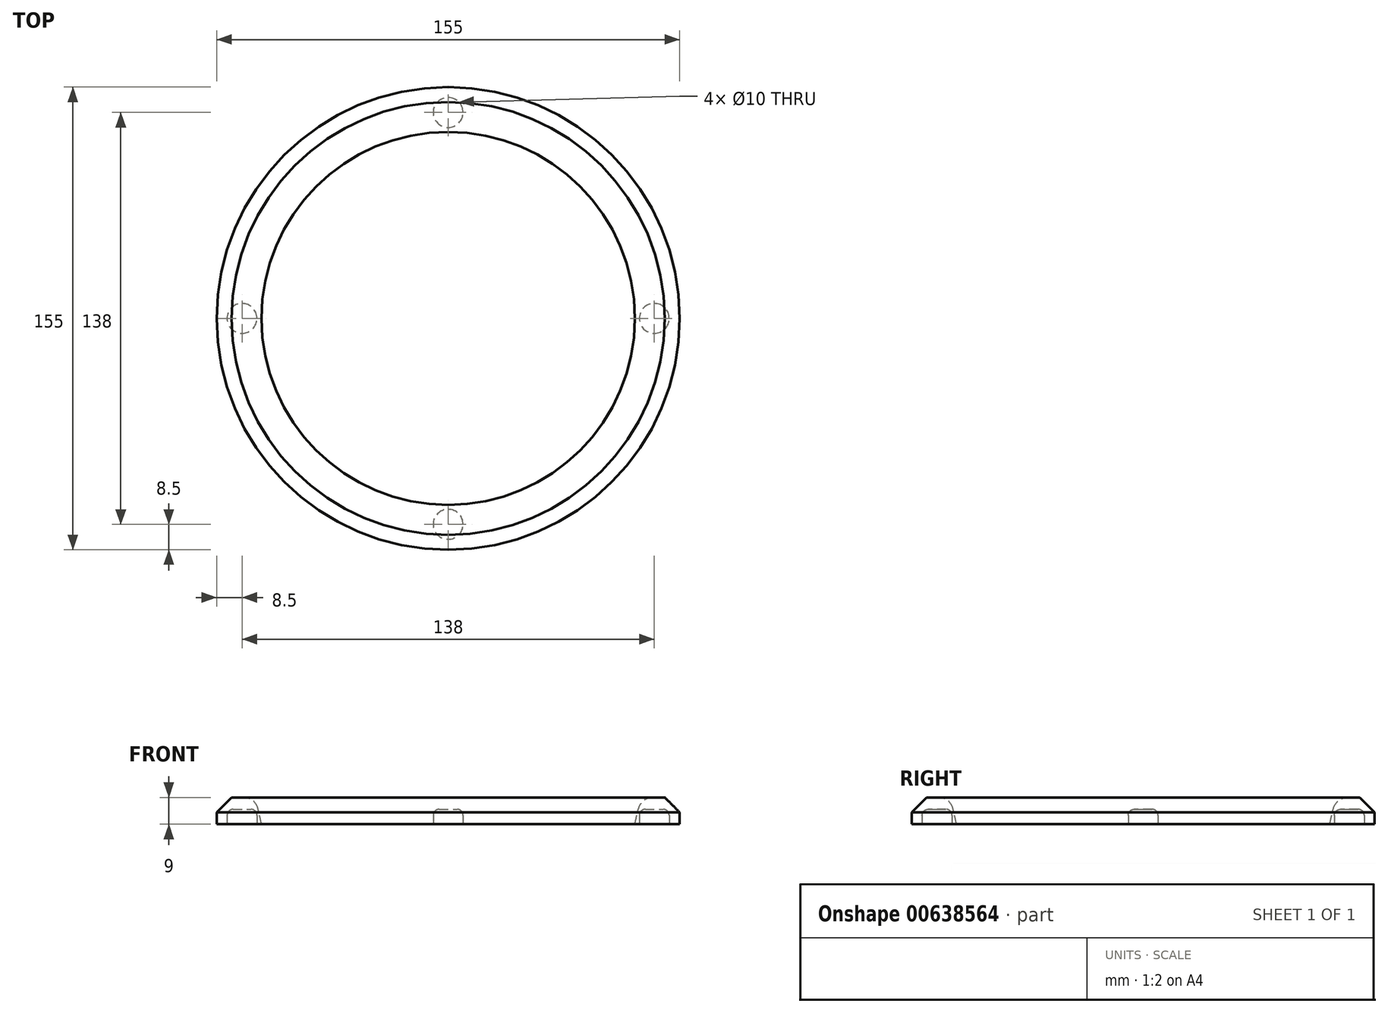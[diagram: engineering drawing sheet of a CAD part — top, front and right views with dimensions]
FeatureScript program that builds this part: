
annotation { "Feature Type Name" : "Feature", "Feature Type Description" : "" }
export const myFeature = defineFeature(function(context is Context, id is Id, definition is map)
    precondition{}
    {
        {
            var Q0;
            Q0=qCreatedBy(makeId("Top.planeOp"),FACE);
            var sketch = newSketch(context, id + "F0", { "sketchPlane" : qUnion([Q0])});
            skCircle(sketch, "E0", {"center": v(0, 0) * mm, "radius": 62.5 * mm});
            skCircle(sketch, "E1.0", {"center": v(0, 0) * mm, "radius": 77.5 * mm});
            skSolve(sketch);
        }
        {
            var Q0;
            Q0 = qSketchRegion(id + "F0", true);
            extrude(context, id + "F1", {"entities" : qUnion([Q0]), "depth" : 9 * mm, "offsetDistance" : 25 * mm});
        }
        {
            var Q0;
            Q0=makeQuery(id+"F1.opExtrude","CAP_EDGE",EDGE,{"disambiguationData":[OSD([sQuery(id+"F0.wireOp",EDGE,"E1.0")])],"isStart":false});
            chamfer(context, id + "F2", {"entities" : qUnion([Q0]), "width" : 5 * mm, "tangentPropagation" : true});
        }
        {
            var Q0;
            Q0=makeQuery(id+"F1.opExtrude","CAP_EDGE",EDGE,{"disambiguationData":[OSD([sQuery(id+"F0.wireOp",EDGE,"E0")])],"isStart":false});
            chamfer(context, id + "F3", {"entities" : qUnion([Q0]), "chamferType" : ChamferType.TWO_OFFSETS, "width1" : 9 * mm, "oppositeDirection" : false, "width2" : 2 * mm, "tangentPropagation" : true});
        }
        {
            var Q0;
            {var subQ0=sQuery(id+"F0.wireOp",EDGE,"E0");Q0=makeQuery(id+"F3.opChamfer","BLEND_EDGE",EDGE,{"blendedFrom":[makeQuery(id+"F1.opExtrude","CAP_EDGE",EDGE,{"disambiguationData":[OSD([subQ0])],"isStart":false}),makeQuery(id+"F1.opExtrude","CAP_FACE",FACE,{"disambiguationData":[OSD([subQ0,sQuery(id+"F0.wireOp",EDGE,"E1.0")])],"isStart":false})],"blendedInto":[makeQuery(id+"F1.opExtrude","CAP_FACE",FACE,{"disambiguationData":[OSD([subQ0,sQuery(id+"F0.wireOp",EDGE,"E1.0")])],"isStart":false})]});}
            fillet(context, id + "F4", {"entities" : qUnion([Q0]), "radius" : 5 * mm, "tangentPropagation" : true, "allowEdgeOverflow" : false});
        }
        {
            var Q0;
            Q0=makeQuery(id+"F1.opExtrude","CAP_FACE",FACE,{"disambiguationData":[OSD([sQuery(id+"F0.wireOp",EDGE,"E0"),sQuery(id+"F0.wireOp",EDGE,"E1.0")])],"isStart":true});
            var sketch = newSketch(context, id + "F5", { "sketchPlane" : qUnion([Q0])});
            skCircle(sketch, "E2", {"center": v(0, 0) * mm, "radius": 69 * mm, "construction": true});
            skCircle(sketch, "E3", {"center": v(0, 69) * mm, "radius": 5 * mm});
            skCircle(sketch, "E4.1.0", {"center": v(-69, 0) * mm, "radius": 5 * mm});
            skCircle(sketch, "E4.2.0", {"center": v(0, -69) * mm, "radius": 5 * mm});
            skCircle(sketch, "E4.3.0", {"center": v(69, 0) * mm, "radius": 5 * mm});
            skSolve(sketch);
        }
        {
            var Q0;
            Q0 = qSketchRegion(id + "F5", true);
            extrude(context, id + "F6", {"entities" : qUnion([Q0]), "operationType" : NewBodyOperationType.REMOVE, "oppositeDirection" : true, "depth" : 5 * mm, "offsetDistance" : 25 * mm});
        }
        {
            var Q0;
            Q0=makeQuery(id+"F6.boolean.opBoolean","COPY",EDGE,{"derivedFrom":makeQuery(id+"F6.opExtrude","CAP_EDGE",EDGE,{"disambiguationData":[OSD([sQuery(id+"F5.wireOp",EDGE,"E3")])],"isStart":false})});
            var Q1;
            Q1=makeQuery(id+"F6.boolean.opBoolean","COPY",EDGE,{"derivedFrom":makeQuery(id+"F6.opExtrude","CAP_EDGE",EDGE,{"disambiguationData":[OSD([sQuery(id+"F5.wireOp",EDGE,"E4.1.0")])],"isStart":false})});
            var Q2;
            Q2=makeQuery(id+"F6.boolean.opBoolean","COPY",EDGE,{"derivedFrom":makeQuery(id+"F6.opExtrude","CAP_EDGE",EDGE,{"disambiguationData":[OSD([sQuery(id+"F5.wireOp",EDGE,"E4.3.0")])],"isStart":false})});
            var Q3;
            Q3=makeQuery(id+"F6.boolean.opBoolean","COPY",EDGE,{"derivedFrom":makeQuery(id+"F6.opExtrude","CAP_EDGE",EDGE,{"disambiguationData":[OSD([sQuery(id+"F5.wireOp",EDGE,"E4.2.0")])],"isStart":false})});
            fillet(context, id + "F7", {"entities" : qUnion([Q0, Q1, Q2, Q3]), "radius" : 2 * mm, "tangentPropagation" : true, "allowEdgeOverflow" : false});
        }
    });
